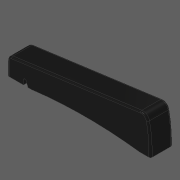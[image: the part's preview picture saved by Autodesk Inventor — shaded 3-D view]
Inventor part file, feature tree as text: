
AUTODESK INVENTOR PART (.ipt)
format: ipt  version: 2020 (Build 240168000, 168)  size: 274,944 bytes
history: native  units: in
note: dims shown in document units (in); Inventor stores cm internally (conversion verified against a paired STEP export)
features: other x4, extrude x3, fillet x2
ambient origin geometry x8: Origin, YZ Plane, XZ Plane, XY Plane, X Axis, Y Axis, Z Axis, Center Point
bodies: Solid1 (feature_tree)
feature tree (9):
  other  "BlackKey0"
  other  "Slot Start Plane"
  other  "Key Profile"
  extrude  "Key"  Depth=0.0787in
  extrude  "Protrusion Cutout"  TaperAngle=0.0deg  [1 undecoded]
  fillet  "Front Fillet"  [1 undecoded]
  extrude  "Slot"  Depth=0.1181in
  fillet  "Edge Softening"  Radius=0.1374in
  other  "Slot Sketch"
note: 2 required parameter values undecoded (feature->parameter linkage not recoverable at this tier; creation-order binding heuristic only, values carry confidence <= 0.55)
